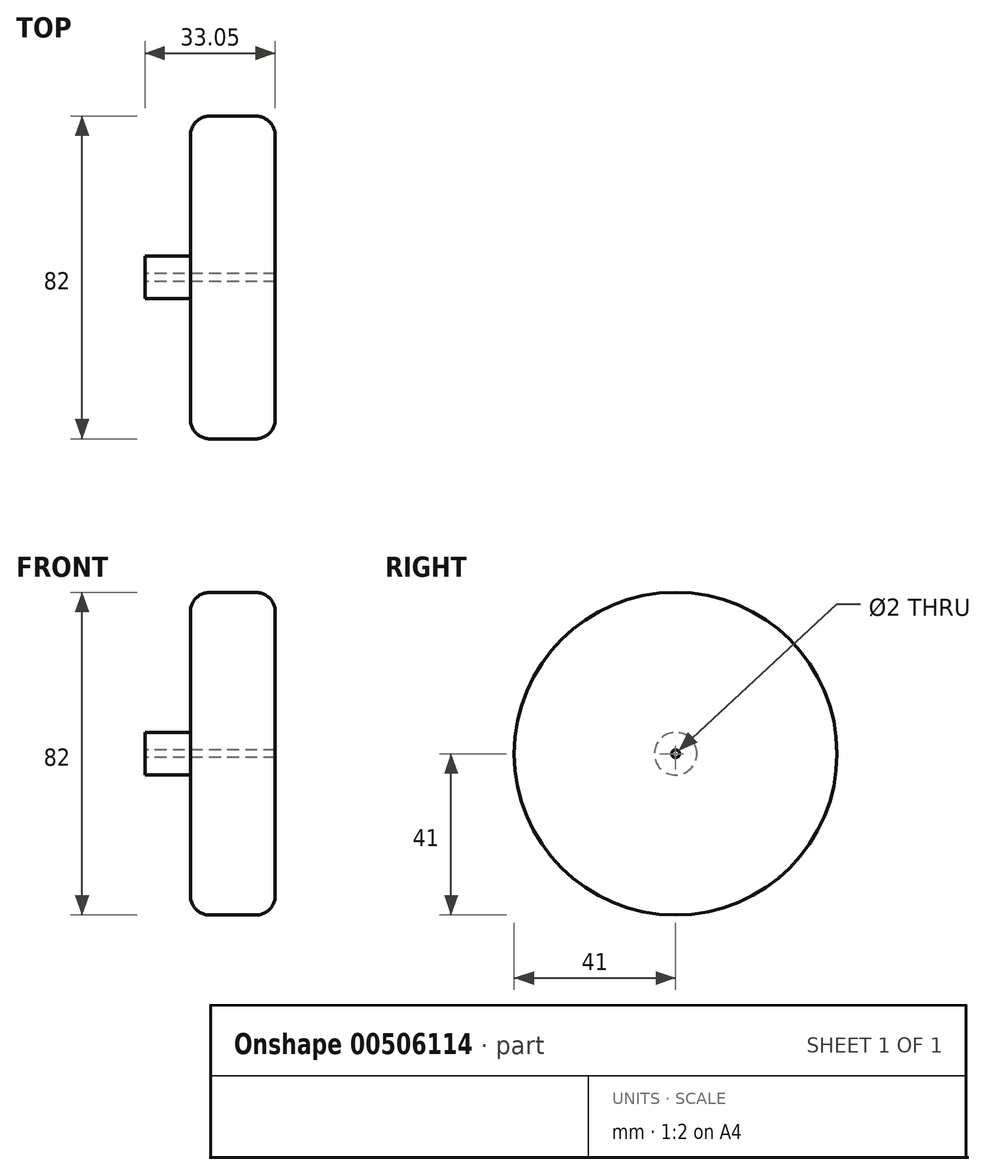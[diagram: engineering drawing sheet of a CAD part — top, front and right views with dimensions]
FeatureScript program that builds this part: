
annotation { "Feature Type Name" : "Feature", "Feature Type Description" : "" }
export const myFeature = defineFeature(function(context is Context, id is Id, definition is map)
    precondition{}
    {
        {
            var Q0;
            Q0=qCreatedBy(makeId("Front.planeOp"),FACE);
            var sketch = newSketch(context, id + "F0", { "sketchPlane" : qUnion([Q0])});
            skLineSegment(sketch, "E0", {"start": v(-84.52, 0) * mm, "end": v(87.98, 0) * mm, "construction": true});
            skLineSegment(sketch, "E1", {"start": v(0, 44.7) * mm, "end": v(0, -42.8) * mm, "construction": true});
            skLineSegment(sketch, "E2.bottom", {"start": v(-11.49, 5.4) * mm, "end": v(0, 5.4) * mm});
            skLineSegment(sketch, "E2.top", {"start": v(-11.49, 1) * mm, "end": v(21.56, 1) * mm});
            skLineSegment(sketch, "E2.left", {"start": v(-11.49, 5.4) * mm, "end": v(-11.49, 1) * mm});
            skLineSegment(sketch, "E3.top", {"start": v(21.56, 41) * mm, "end": v(0, 41) * mm});
            skLineSegment(sketch, "E3.right", {"start": v(0, 5.4) * mm, "end": v(0, 41) * mm});
            skLineSegment(sketch, "E4", {"start": v(21.56, 1) * mm, "end": v(21.56, 41) * mm});
            skSolve(sketch);
        }
        {
            var Q0;
            Q0=makeQuery(id+"F0.imprint","IMPRINT",FACE,{"disambiguationData":[TD([[makeQuery(id+"F0.imprint","IMPRINT",EDGE,{"derivedFrom":sQuery(id+"F0.wireOp",EDGE,"E2.bottom")}),-1.0]])]});
            var Q1;
            Q1 = qSketchRegion(id + "FvaAl5dQStMehDQ_0", true);
            var Q2;
            Q2=sQuery(id+"F0.wireOp",EDGE,"E0");
            revolve(context, id + "F1", {"entities" : qUnion([Q0, Q1]), "axis" : qUnion([Q2]), "revolveType" : RevolveType.FULL});
        }
        {
            var Q0;
            Q0=makeQuery(id+"F1.opRevolve","SWEPT_EDGE",EDGE,{"disambiguationData":[OSD([sQuery(id+"F0.wireOp",EDGE,"E3.top"),sQuery(id+"F0.wireOp",EDGE,"E4")])]});
            var Q1;
            Q1=makeQuery(id+"F1.opRevolve","SWEPT_EDGE",EDGE,{"disambiguationData":[OSD([sQuery(id+"F0.wireOp",EDGE,"E3.top"),sQuery(id+"F0.wireOp",EDGE,"E3.right")])]});
            fillet(context, id + "F2", {"entities" : qUnion([Q0, Q1]), "radius" : 5 * mm, "tangentPropagation" : true, "allowEdgeOverflow" : false});
        }
    });
